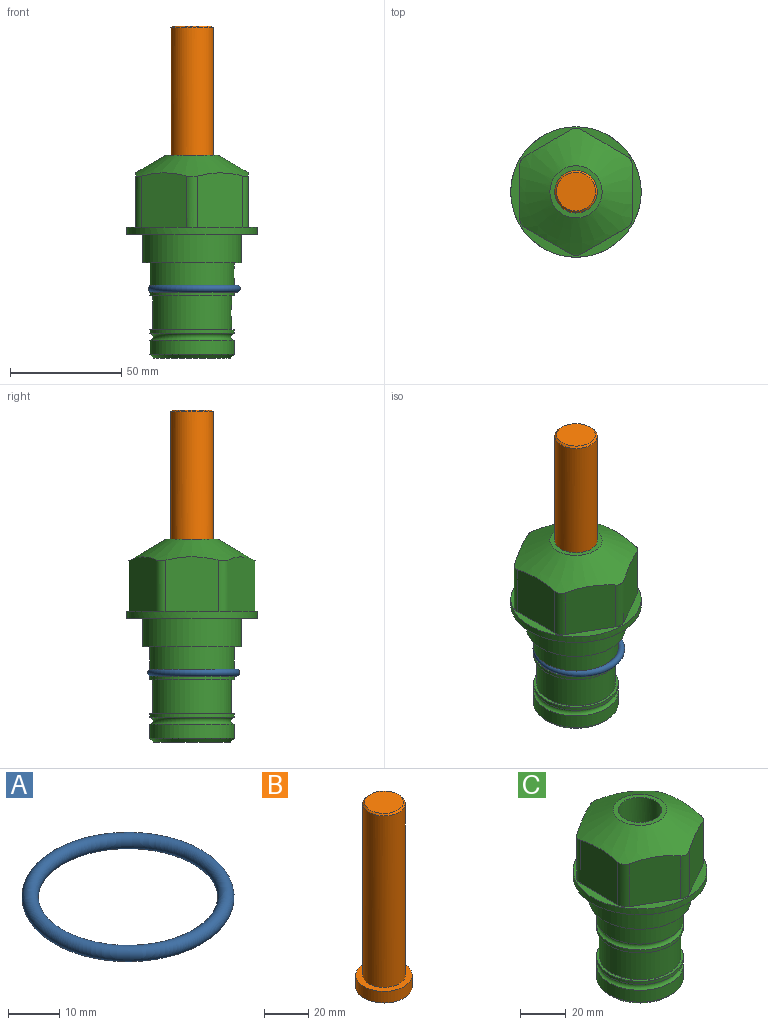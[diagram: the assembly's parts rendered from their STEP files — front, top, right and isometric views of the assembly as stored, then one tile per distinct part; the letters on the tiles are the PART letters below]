
ASSEMBLY  parts=3 mates=1
PART A: 1 faces, bbox 44.7x44.7x3.2 mm
  f0: torus R=19.05mm, axis (0,0,1), area 1193.9mm2
PART B: 6 faces, bbox 25.4x25.4x101.6 mm
  f0: plane 17.46x17.46mm, normal (0,0,1), area 239.5mm2, adj f5
  f1: plane 25.4x25.4mm, normal (0,0,-1), area 506.7mm2, adj f2
  f2: cylinder r=12.7mm len=25.4mm, axis (0,0,1), area 506.7mm2, adj f1,f3
  f3: plane 25.4x25.4mm, normal (0,0,1), area 221.7mm2, adj f2,f4
  f4: cylinder r=9.53mm len=94.46mm, axis (0,0,1), area 5653mm2, adj f3,f5
  f5: cone r=8.73mm half-angle=45deg, axis (0,0,-1), area 64.4mm2, adj f0,f4
PART C: 36 faces, bbox 58.7x58.7x91.2 mm
  f0: cylinder r=17.78mm len=35.56mm, axis (0,0,1), area 1670.8mm2, adj f23,f24,f31
  f1: cylinder r=19.05mm len=38.1mm, axis (0,0,1), area 1191.9mm2, adj f26,f27,f30
  f2: plane 58.66x58.66mm, normal (0,0,-1), area 1150.6mm2, adj f3,f28
  f3: cylinder r=29.33mm len=58.66mm, axis (0,0,-1), area 585.1mm2, adj f2,f4
  f4: plane 58.66x58.66mm, normal (0,0,1), area 475.9mm2, adj f3,f5,f6,f7,f8,f9,f10,f11
  f5: plane 24.5x20.32mm, normal (-0.5,0.87,0), area 562.8mm2, adj f4,f15,f16,f17
  f6: plane 24.5x20.32mm, normal (0.5,0.87,0), area 562.8mm2, adj f4,f14,f15,f17
  f7: plane 24.5x23.48mm, normal (1,0,0), area 562.8mm2, adj f4,f13,f14,f17
  f8: plane 24.5x20.32mm, normal (0.5,-0.87,0), area 562.8mm2, adj f4,f12,f13,f17
  f9: plane 24.5x20.32mm, normal (-0.5,-0.87,0), area 562.8mm2, adj f4,f11,f12,f17
  f10: plane 24.5x23.48mm, normal (-1,0,0), area 562.8mm2, adj f4,f11,f16,f17
  f11: cylinder r=5.08mm len=23.01mm, axis (0,0,-1), area 121.2mm2, adj f4,f9,f10,f17
  f12: cylinder r=5.08mm len=23.01mm, axis (0,0,-1), area 121.2mm2, adj f4,f8,f9,f17
  f13: cylinder r=5.08mm len=23.01mm, axis (0,0,-1), area 121.2mm2, adj f4,f7,f8,f17
  f14: cylinder r=5.08mm len=23.01mm, axis (0,0,-1), area 121.2mm2, adj f4,f6,f7,f17
  f15: cylinder r=5.08mm len=23.01mm, axis (0,0,-1), area 121.2mm2, adj f4,f5,f6,f17
  f16: cylinder r=5.08mm len=23.01mm, axis (0,0,-1), area 121.2mm2, adj f4,f5,f10,f17
  f17: cone r=11.73mm half-angle=60deg, axis (0,0,-1), area 2071.8mm2, adj f5,f6,f7,f8,f9,f10,f11,f12
  f18: plane 23.46x23.46mm, normal (0,0,1), area 147.4mm2, adj f17,f35
  f19: plane 34.93x34.93mm, normal (0,0,-1), area 958mm2, adj f29
  f20: cylinder r=19.05mm len=38.1mm, axis (0,0,1), area 760.1mm2, adj f21,f29
  f21: torus R=19.05mm, axis (0,0,1), area 565.3mm2, adj f20,f22
  f22: cylinder r=19.05mm len=38.1mm, axis (0,0,1), area 190mm2, adj f21,f23
  f23: plane 38.1x38.1mm, normal (0,0,1), area 146.9mm2, adj f0,f22
  f24: plane 38.1x38.1mm, normal (0,0,-1), area 146.9mm2, adj f0,f25
  f25: cylinder r=19.05mm len=38.1mm, axis (0,0,1), area 190mm2, adj f24,f26
  f26: torus R=19.05mm, axis (0,0,1), area 565.3mm2, adj f1,f25
  f27: plane 44.45x44.45mm, normal (0,0,-1), area 411.7mm2, adj f1,f28
  f28: cylinder r=22.23mm len=44.45mm, axis (0,0,1), area 1773.5mm2, adj f2,f27
  f29: cone r=19.05mm half-angle=45deg, axis (0,0,1), area 257.5mm2, adj f19,f20
  f30: cylinder r=3.17mm len=6.75mm, axis (-1,0,0), area 128mm2, adj f1,f33
  f31: cylinder r=3.17mm len=6.35mm, axis (-1,0,0), area 102.5mm2, adj f0,f33
  f32: plane 25.4x25.4mm, normal (0,0,1), area 506.7mm2, adj f33
  f33: cylinder r=12.7mm len=66.42mm, axis (0,0,-1), area 5236.2mm2, adj f30,f31,f32,f34
  f34: cone r=9.53mm half-angle=30deg, axis (0,0,-1), area 443.4mm2, adj f33,f35
  f35: cylinder r=9.53mm len=19.05mm, axis (0,0,-1), area 849mm2, adj f18,f34
PLACE A t=(-27.4,2.49,-30.88)mm
PLACE B t=(-28.45,3.25,-10.96)mm
PLACE C t=(-28.45,3.25,-31)mm
MATE cylindrical B.f2 <-> C.f0  axis (0,0,1) through (-28.45,3.25,62.7)mm
